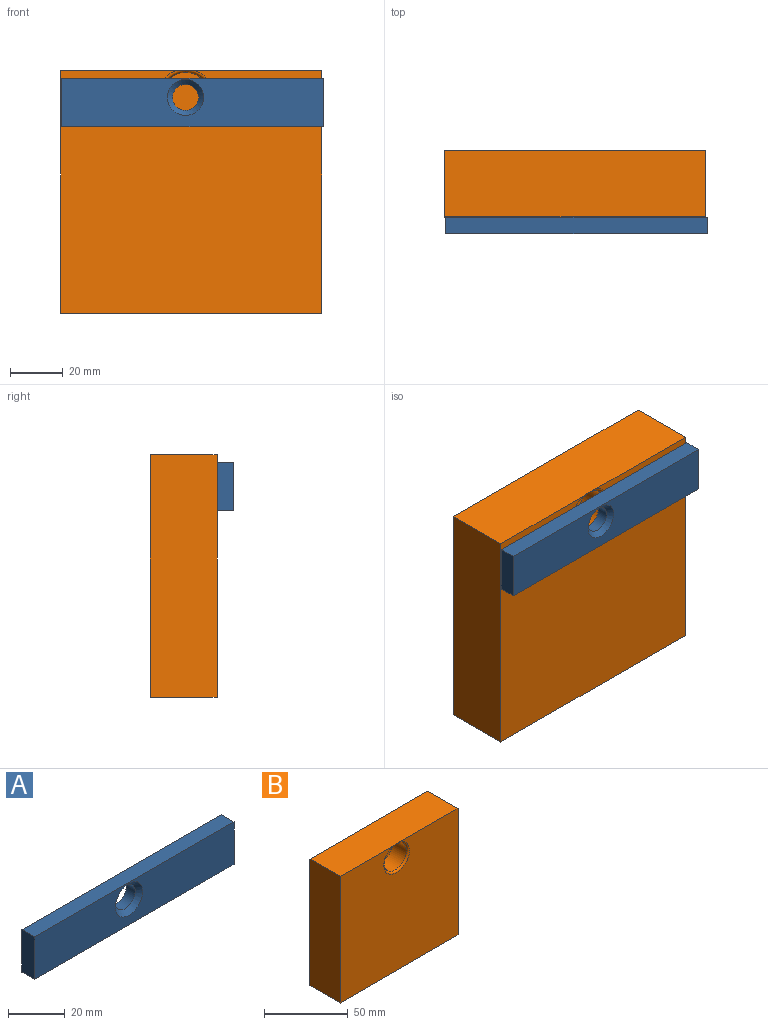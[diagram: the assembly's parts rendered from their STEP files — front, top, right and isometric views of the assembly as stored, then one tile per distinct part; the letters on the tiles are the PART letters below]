
ASSEMBLY  parts=2 mates=1
PART A: 8 faces, bbox 99.6x6.4x18.4 mm
  f0: plane 18.37x6.35mm, normal (-1,0,0), area 116.6mm2, adj f1,f3,f4,f5
  f1: plane 99.6x6.35mm, normal (0,0,-1), area 632.5mm2, adj f0,f2,f4,f5
  f2: plane 18.37x6.35mm, normal (1,0,0), area 116.6mm2, adj f1,f3,f4,f5
  f3: plane 99.6x6.35mm, normal (0,0,1), area 632.5mm2, adj f0,f2,f4,f5
  f4: plane 99.6x18.37mm, normal (0,-1,0), area 1681.8mm2, adj f0,f1,f2,f3,f7
  f5: plane 99.6x18.37mm, normal (0,1,0), area 1752.5mm2, adj f0,f1,f2,f3,f6
  f6: cylinder r=4.96mm len=9.91mm, axis (0,1,0), area 138.4mm2, adj f5,f7
  f7: cone r=6.86mm half-angle=45deg, axis (0,-1,0), area 100mm2, adj f4,f6
PART B: 9 faces, bbox 99.3x25.4x94.8 mm
  f0: plane 92.32x25.4mm, normal (-1,0,0), area 2345mm2, adj f1,f3,f4,f5
  f1: plane 99.28x25.4mm, normal (0,0,-1), area 2521.6mm2, adj f0,f2,f4,f5
  f2: plane 92.32x25.4mm, normal (1,0,0), area 2345mm2, adj f1,f3,f4,f5
  f3: plane 99.28x25.4mm, normal (0,0,1), area 2521mm2, adj f0,f2,f4,f5,f8
  f4: plane 99.28x92.32mm, normal (0,-1,0), area 8802.4mm2, adj f0,f1,f2,f3,f8
  f5: plane 99.28x92.32mm, normal (0,1,0), area 9165.4mm2, adj f0,f1,f2,f3
  f6: cylinder r=9.53mm len=19.05mm, axis (0,-1,0), area 684.1mm2, adj f7,f8
  f7: plane 19.05x19.05mm, normal (0,-1,0), area 285mm2, adj f6
  f8: torus R=10.79mm, axis (0,-1,0), area 122mm2, adj f3,f4,f6
PLACE A t=(-0.2,-25.4,95.64)mm
PLACE B at identity
MATE fastened A.f6 <-> B.f6  axis (0,1,0) through (-0.2,-25.4,39.79)mm
